# Revit family: 304_6671a74a2b704780975e46da077cee
name_source: partatom
category: Pipe Accessories
units: mm (PartAtom-declared; Revit-internal decimal feet)

## family parameters
Always vertical = Yes
Cut with Voids When Loaded = No
Part Type = Valve - Breaks Into
Round Connector Dimension = Use Diameter
Shared = No
Work Plane-Based = No

## types (9) — shared parameters
A3WP = 112 mm
ACT1 = Yes
ACT2 = No
ACT2L = 230 mm
ACT3 = No
ACT3L = 93 mm
ACT3W = 167 mm
AL2 = 156 mm
CAT0 = Yes
Description = Pressure independent control valve
L2D = 350 mm
L2D_Min = 3048 mm
Manufacturer = Frese A/S
QmdConnectorList = 301;D;302;D
URL = https://www.frese.eu
W2D = 100 mm
magiPartTypeId = 304
magiProductFamilyId = 6671a74a2b704780975e46da077cee

## per-type parameters (varying)
| type | ACT2H | D | DD | DF2 | H | H1 | H2 | H3 | H4 | H6 | L2 | L3 | L4 | LF | LF2 | LF__ve | R1 | R3 | R4 | magiProductId |
| Frese Optima Compact Low flow PN25 DN100 | 289 mm | 100 mm | No | 118 mm | 700 mm | 176 mm | 88 mm | 29 mm | 35 mm  [stored 0.114829 ft] | 186 mm | 175 mm | 294 mm | 165 mm | 28 mm  [stored 0.0918635 ft] | 14 mm  [stored 0.0459318 ft] | -28 mm  [stored -0.0918635 ft] | 88 mm | 61 mm  [stored 0.200131 ft] | 61 mm  [stored 0.200131 ft] | c01a2dbd7df9417e9cc91d86eb7067 |
| Frese Optima Compact Low flow PN25 DN125 | 289 mm | 125 mm | No | 135 mm | 747 mm | 203 mm | 101 mm | 34 mm  [stored 0.111549 ft] | 41 mm  [stored 0.134514 ft] | 193 mm | 200 mm | 336 mm | 188 mm | 32 mm  [stored 0.104987 ft] | 16 mm  [stored 0.0524934 ft] | -32 mm  [stored -0.104987 ft] | 100 mm | 70 mm | 70 mm | 5d08dc6b93cd4a009f938f2698c221 |
| Frese Optima Compact Low flow PN25 DN150 | 289 mm | 150 mm | No | 143 mm | 768 mm | 214 mm | 107 mm | 36 mm | 43 mm | 196 mm | 240 mm | 403 mm | 226 mm | 38 mm | 19 mm | -38 mm | 120 mm | 74 mm | 84 mm | eef20d30fed94612b024ae0497585f |
| Frese Optima Compact Low flow PN25 DN200 | 289 mm | 200 mm | Yes | 190 mm | 840 mm | 380 mm | 209 mm | 15 mm  [stored 0.0492126 ft] | 57 mm | 159 mm | 300 mm | 504 mm | 282 mm | 48 mm  [stored 0.15748 ft] | 24 mm  [stored 0.0787402 ft] | -48 mm  [stored -0.15748 ft] | 235 mm | 99 mm | 165 mm | 62e554e25bbb433a90a84090255505 |
| Frese Optima Compact Low flow PN25 DN250 | 311 mm | 250 mm | Yes | 222 mm | 1094 mm | 444 mm | 244 mm | 15 mm  [stored 0.0492126 ft] | 67 mm  [stored 0.219816 ft] | 339 mm | 365 mm | 613 mm | 343 mm | 58 mm | 29 mm | -58 mm | 275 mm | 115 mm | 192 mm | 20821eea46024d2fbc17bc30e76bb6 |
| Frese Optima Compact Low flow PN25 DN300 | 311 mm | 300 mm | Yes | 260 mm | 1132 mm | 520 mm | 286 mm | 15 mm  [stored 0.0492126 ft] | 78 mm | 290 mm | 425 mm | 714 mm | 400 mm | 68 mm | 34 mm  [stored 0.111549 ft] | -68 mm  [stored -0.223097 ft] | 360 mm | 135 mm | 252 mm | 927549d0afbe43c2b0a2f05f2749bf |
| Frese Optima Compact Low flow PN25 DN50 | 289 mm | 50 mm | No | 83 mm | 508 mm | 124 mm | 62 mm | 21 mm | 25 mm  [stored 0.082021 ft] | 74 mm | 115 mm | 193 mm | 108 mm | 18 mm | 9 mm | -18 mm | 58 mm | 43 mm | 40 mm  [stored 0.131234 ft] | 679de7d54afb45d9868404793f65be |
| Frese Optima Compact Low flow PN25 DN65 | 289 mm | 65 mm | No | 93 mm | 525 mm | 139 mm | 69 mm | 23 mm | 28 mm  [stored 0.0918635 ft] | 68 mm | 145 mm | 244 mm | 136 mm | 23 mm | 12 mm  [stored 0.0393701 ft] | -23 mm | 73 mm | 48 mm  [stored 0.15748 ft] | 51 mm | a8bc4041806b4938975dab9e4a7324 |
| Frese Optima Compact Low flow PN25 DN80 | 289 mm | 80 mm | No | 100 mm | 554 mm | 150 mm | 75 mm | 25 mm  [stored 0.082021 ft] | 30 mm  [stored 0.0984252 ft] | 80 mm | 155 mm | 260 mm | 146 mm | 25 mm  [stored 0.082021 ft] | 12 mm  [stored 0.0393701 ft] | -25 mm  [stored -0.082021 ft] | 78 mm | 52 mm  [stored 0.170604 ft] | 54 mm  [stored 0.177165 ft] | 915089677aaf4d3b8c65c79d95dc8e |

note: column(s) folded — value = type name in every type: MC Product Code

note: [stored X ft] marks values corroborated as IEEE doubles in the binary element streams (Revit-internal decimal feet)
